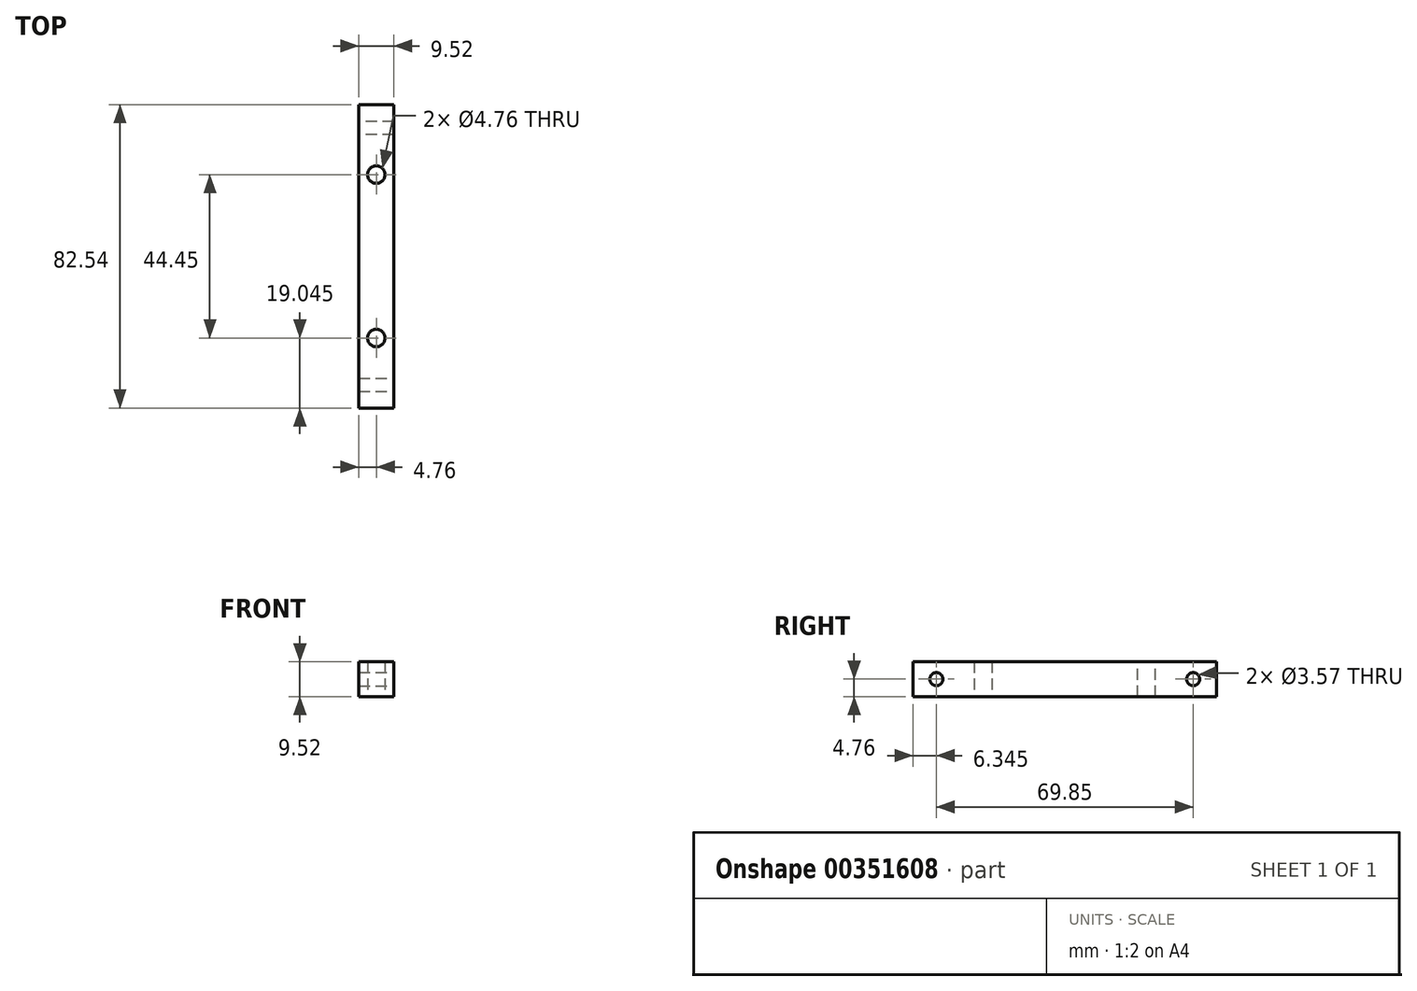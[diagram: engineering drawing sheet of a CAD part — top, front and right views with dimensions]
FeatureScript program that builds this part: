
annotation { "Feature Type Name" : "Feature", "Feature Type Description" : "" }
export const myFeature = defineFeature(function(context is Context, id is Id, definition is map)
    precondition{}
    {
        {
            var Q0;
            Q0=qCreatedBy(makeId("Front.planeOp"),FACE);
            var sketch = newSketch(context, id + "F0", { "sketchPlane" : qUnion([Q0])});
            skLineSegment(sketch, "E0.bottom", {"start": v(-4.76, 4.76) * mm, "end": v(4.76, 4.76) * mm});
            skLineSegment(sketch, "E0.top", {"start": v(-4.76, -4.76) * mm, "end": v(4.76, -4.76) * mm});
            skLineSegment(sketch, "E0.left", {"start": v(-4.76, 4.76) * mm, "end": v(-4.76, -4.76) * mm});
            skLineSegment(sketch, "E0.right", {"start": v(4.76, 4.76) * mm, "end": v(4.76, -4.76) * mm});
            skPoint(sketch, "E0.middle", {"position": v(0, 0) * mm});
            skSolve(sketch);
        }
        {
            var Q0;
            Q0 = qSketchRegion(id + "F0", true);
            extrude(context, id + "F1", {"entities" : qUnion([Q0]), "depth" : 82.55 * mm, "symmetric" : true});
        }
        {
            var Q0;
            Q0=qCreatedBy(makeId("Right.planeOp"),FACE);
            var sketch = newSketch(context, id + "F2", { "sketchPlane" : qUnion([Q0])});
            skCircle(sketch, "E1", {"center": v(-34.93, 0) * mm, "radius": 1.79 * mm});
            skSolve(sketch);
        }
        {
            var Q0;
            Q0 = qSketchRegion(id + "F2", true);
            extrude(context, id + "F3", {"entities" : qUnion([Q0]), "operationType" : NewBodyOperationType.REMOVE, "oppositeDirection" : true, "depth" : 25.4 * mm, "symmetric" : true});
        }
        {
            var Q0;
            Q0=makeQuery(id+"F1.opExtrude","SWEPT_FACE",FACE,{"disambiguationData":[OSD([sQuery(id+"F0.wireOp",EDGE,"E0.right")])]});
            var sketch = newSketch(context, id + "F4", { "sketchPlane" : qUnion([Q0])});
            skCircle(sketch, "E2", {"center": v(34.93, 0) * mm, "radius": 1.79 * mm});
            skSolve(sketch);
        }
        {
            var Q0;
            Q0 = qSketchRegion(id + "F4", true);
            extrude(context, id + "F5", {"entities" : qUnion([Q0]), "operationType" : NewBodyOperationType.REMOVE, "depth" : 25.4 * mm, "symmetric" : true});
        }
        {
            var Q0;
            Q0=qCreatedBy(makeId("Top.planeOp"),FACE);
            var sketch = newSketch(context, id + "F6", { "sketchPlane" : qUnion([Q0])});
            skCircle(sketch, "E3", {"center": v(0, -22.23) * mm, "radius": 2.38 * mm});
            skSolve(sketch);
        }
        {
            var Q0;
            Q0 = qSketchRegion(id + "F6", true);
            extrude(context, id + "F7", {"entities" : qUnion([Q0]), "operationType" : NewBodyOperationType.REMOVE, "depth" : 25.4 * mm, "symmetric" : true});
        }
        {
            var Q0;
            Q0=makeQuery(id+"F1.opExtrude","SWEPT_FACE",FACE,{"disambiguationData":[OSD([sQuery(id+"F0.wireOp",EDGE,"E0.bottom")])]});
            var sketch = newSketch(context, id + "F8", { "sketchPlane" : qUnion([Q0])});
            skCircle(sketch, "E4", {"center": v(0, 22.23) * mm, "radius": 2.38 * mm});
            skSolve(sketch);
        }
        {
            var Q0;
            Q0 = qSketchRegion(id + "F8", true);
            extrude(context, id + "F9", {"entities" : qUnion([Q0]), "operationType" : NewBodyOperationType.REMOVE, "oppositeDirection" : true, "depth" : 25.4 * mm, "symmetric" : true});
        }
    });
